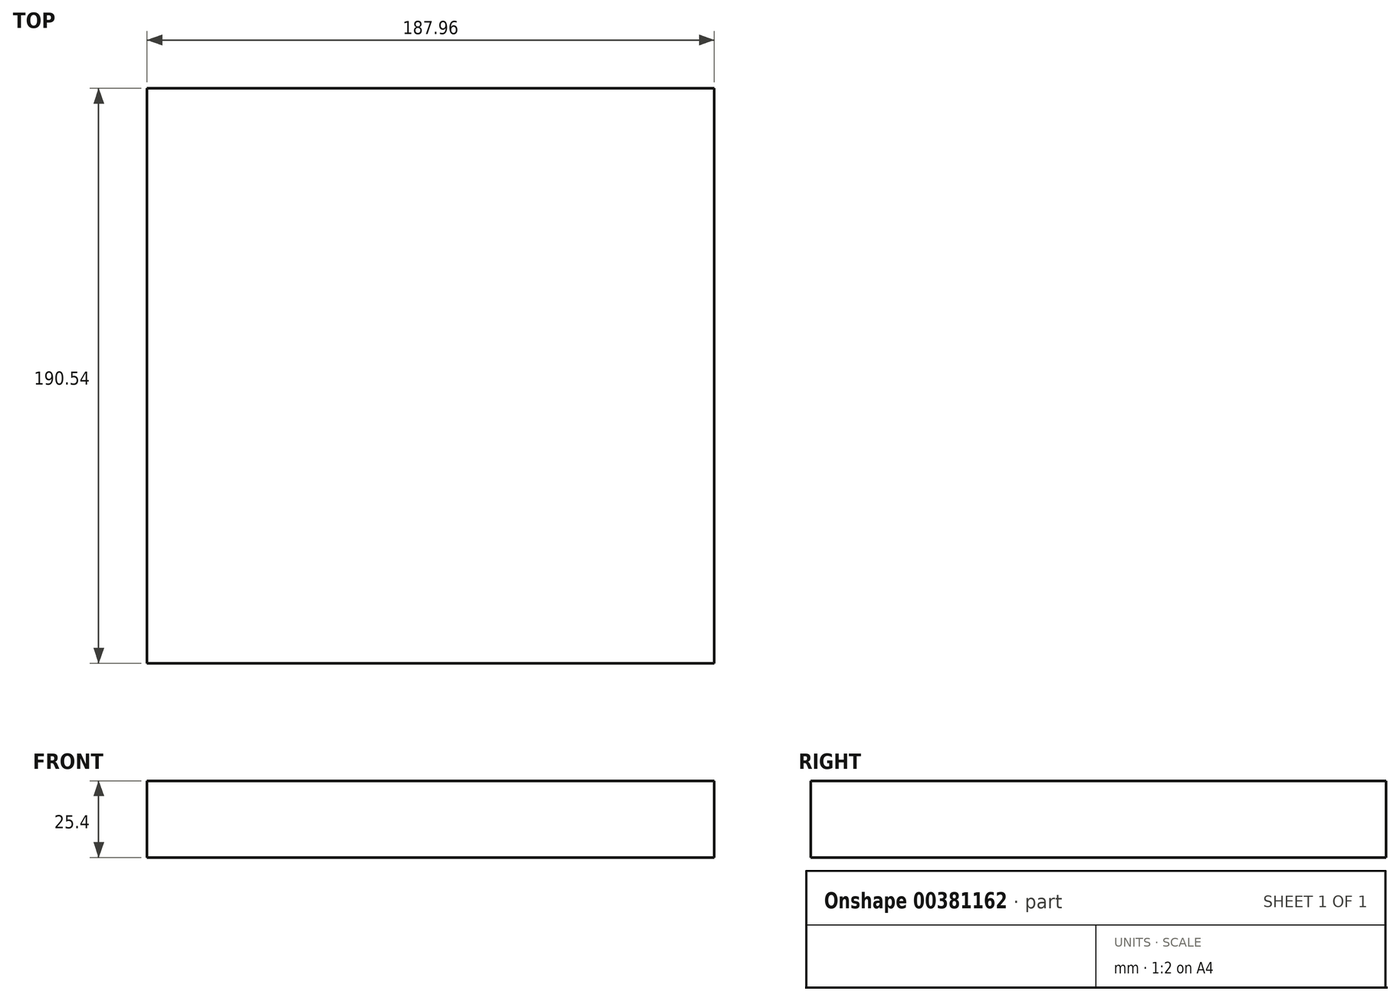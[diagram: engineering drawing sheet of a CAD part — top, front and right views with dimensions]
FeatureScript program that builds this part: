
annotation { "Feature Type Name" : "Feature", "Feature Type Description" : "" }
export const myFeature = defineFeature(function(context is Context, id is Id, definition is map)
    precondition{}
    {
        {
            var Q0;
            Q0=qCreatedBy(makeId("Top.planeOp"),FACE);
            var sketch = newSketch(context, id + "F0", { "sketchPlane" : qUnion([Q0])});
            skLineSegment(sketch, "E0.bottom", {"start": v(93.98, 95.27) * mm, "end": v(-93.98, 95.27) * mm});
            skLineSegment(sketch, "E0.top", {"start": v(93.98, -95.27) * mm, "end": v(-93.98, -95.27) * mm});
            skLineSegment(sketch, "E0.left", {"start": v(93.98, 95.27) * mm, "end": v(93.98, -95.27) * mm});
            skLineSegment(sketch, "E0.right", {"start": v(-93.98, 95.27) * mm, "end": v(-93.98, -95.27) * mm});
            skPoint(sketch, "E0.middle", {"position": v(0, 0) * mm});
            skSolve(sketch);
        }
        {
            var Q0;
            Q0 = qSketchRegion(id + "F0", true);
            extrude(context, id + "F1", {"entities" : qUnion([Q0]), "depth" : 25.4 * mm});
        }
    });
